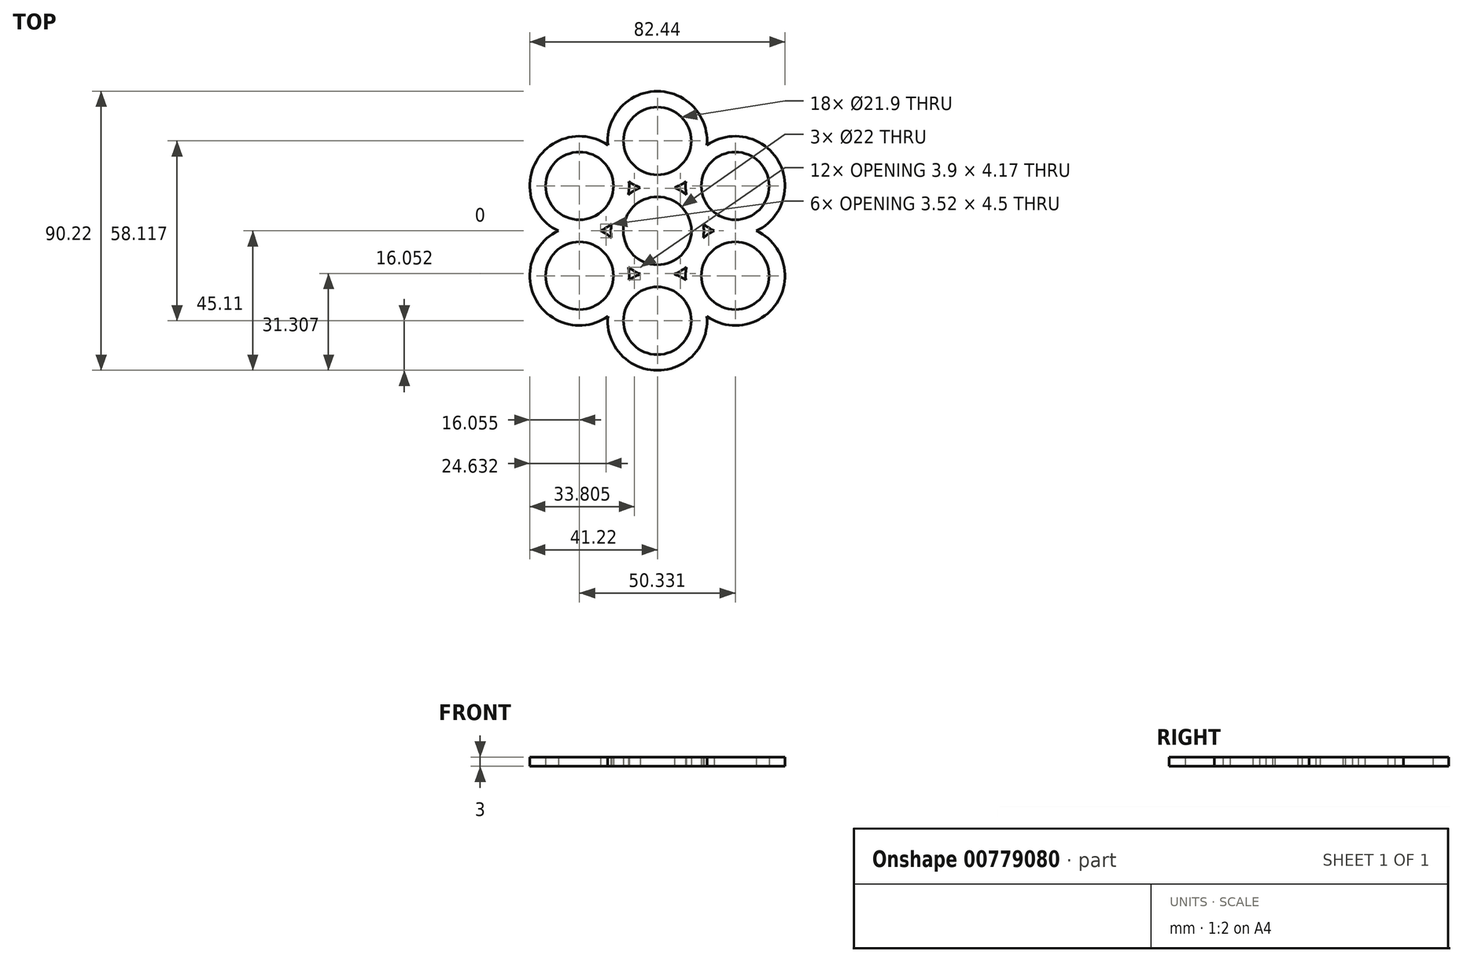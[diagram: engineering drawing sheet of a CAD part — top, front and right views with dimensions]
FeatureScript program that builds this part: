
annotation { "Feature Type Name" : "Feature", "Feature Type Description" : "" }
export const myFeature = defineFeature(function(context is Context, id is Id, definition is map)
    precondition{}
    {
        {
            var Q0;
            Q0=qCreatedBy(makeId("Top.planeOp"),FACE);
            var sketch = newSketch(context, id + "F0", { "sketchPlane" : qUnion([Q0])});
            skArc(sketch, "E0", {"start": v(5.5, 9.53) * mm, "mid": v(0, 11) * mm, "end": v(-5.5, 9.53) * mm});
            skArc(sketch, "E1", {"start": v(7.5, 13) * mm, "mid": v(6.5, 13.52) * mm, "end": v(5.47, 13.97) * mm});
            skCircle(sketch, "E2", {"center": v(0, 29.06) * mm, "radius": 10.95 * mm});
            skArc(sketch, "E3", {"start": v(16, 27.7) * mm, "mid": v(0, 45.1) * mm, "end": v(-16, 27.7) * mm});
            skArc(sketch, "E4.trimOffspring", {"start": v(-9.17, 15.89) * mm, "mid": v(-7.38, 14.8) * mm, "end": v(-5.47, 13.97) * mm});
            skArc(sketch, "E5.trimOffspring", {"start": v(5.47, 13.97) * mm, "mid": v(7.38, 14.8) * mm, "end": v(9.17, 15.89) * mm});
            skArc(sketch, "E6.trimOffspring", {"start": v(-5.47, 13.97) * mm, "mid": v(-6.5, 13.52) * mm, "end": v(-7.5, 13) * mm});
            skCircle(sketch, "E7.1.0", {"center": v(-25.17, 14.53) * mm, "radius": 10.95 * mm});
            skArc(sketch, "E7.1.1", {"start": v(-16, 27.7) * mm, "mid": v(-39.07, 22.55) * mm, "end": v(-31.98, 0) * mm});
            skArc(sketch, "E7.1.2", {"start": v(-9.36, 11.72) * mm, "mid": v(-9.13, 13.8) * mm, "end": v(-9.17, 15.89) * mm});
            skArc(sketch, "E7.1.3", {"start": v(-7.5, 13) * mm, "mid": v(-8.46, 12.39) * mm, "end": v(-9.36, 11.72) * mm});
            skArc(sketch, "E7.1.4", {"start": v(-5.5, 9.53) * mm, "mid": v(-9.53, 5.5) * mm, "end": v(-11, 0) * mm});
            skArc(sketch, "E7.1.5", {"start": v(-14.83, 2.25) * mm, "mid": v(-14.96, 1.13) * mm, "end": v(-15, 0) * mm});
            skArc(sketch, "E7.1.6", {"start": v(-18.35, 0) * mm, "mid": v(-16.51, 1) * mm, "end": v(-14.83, 2.25) * mm});
            skCircle(sketch, "E7.2.0", {"center": v(-25.17, -14.53) * mm, "radius": 10.95 * mm});
            skArc(sketch, "E7.2.1", {"start": v(-31.98, 0) * mm, "mid": v(-39.07, -22.55) * mm, "end": v(-16, -27.7) * mm});
            skArc(sketch, "E7.2.2", {"start": v(-14.83, -2.25) * mm, "mid": v(-16.51, -1) * mm, "end": v(-18.35, 0) * mm});
            skArc(sketch, "E7.2.3", {"start": v(-15, 0) * mm, "mid": v(-14.96, -1.13) * mm, "end": v(-14.83, -2.25) * mm});
            skArc(sketch, "E7.2.4", {"start": v(-11, 0) * mm, "mid": v(-9.53, -5.5) * mm, "end": v(-5.5, -9.53) * mm});
            skArc(sketch, "E7.2.5", {"start": v(-9.36, -11.72) * mm, "mid": v(-8.46, -12.39) * mm, "end": v(-7.5, -13) * mm});
            skArc(sketch, "E7.2.6", {"start": v(-9.17, -15.89) * mm, "mid": v(-9.13, -13.8) * mm, "end": v(-9.36, -11.72) * mm});
            skCircle(sketch, "E7.3.0", {"center": v(0, -29.06) * mm, "radius": 10.95 * mm});
            skArc(sketch, "E7.3.1", {"start": v(-16, -27.7) * mm, "mid": v(0, -45.1) * mm, "end": v(16, -27.7) * mm});
            skArc(sketch, "E7.3.2", {"start": v(-5.47, -13.97) * mm, "mid": v(-7.38, -14.8) * mm, "end": v(-9.17, -15.89) * mm});
            skArc(sketch, "E7.3.3", {"start": v(-7.5, -13) * mm, "mid": v(-6.5, -13.52) * mm, "end": v(-5.47, -13.97) * mm});
            skArc(sketch, "E7.3.4", {"start": v(-5.5, -9.53) * mm, "mid": v(0, -11) * mm, "end": v(5.5, -9.53) * mm});
            skArc(sketch, "E7.3.5", {"start": v(5.47, -13.97) * mm, "mid": v(6.5, -13.52) * mm, "end": v(7.5, -13) * mm});
            skArc(sketch, "E7.3.6", {"start": v(9.17, -15.89) * mm, "mid": v(7.38, -14.8) * mm, "end": v(5.47, -13.97) * mm});
            skCircle(sketch, "E7.4.0", {"center": v(25.17, -14.53) * mm, "radius": 10.95 * mm});
            skArc(sketch, "E7.4.1", {"start": v(16, -27.7) * mm, "mid": v(39.07, -22.55) * mm, "end": v(31.98, 0) * mm});
            skArc(sketch, "E7.4.2", {"start": v(9.36, -11.72) * mm, "mid": v(9.13, -13.8) * mm, "end": v(9.17, -15.89) * mm});
            skArc(sketch, "E7.4.3", {"start": v(7.5, -13) * mm, "mid": v(8.46, -12.39) * mm, "end": v(9.36, -11.72) * mm});
            skArc(sketch, "E7.4.4", {"start": v(5.5, -9.53) * mm, "mid": v(9.53, -5.5) * mm, "end": v(11, 0) * mm});
            skArc(sketch, "E7.4.5", {"start": v(14.83, -2.25) * mm, "mid": v(14.96, -1.13) * mm, "end": v(15, 0) * mm});
            skArc(sketch, "E7.4.6", {"start": v(18.35, 0) * mm, "mid": v(16.51, -1) * mm, "end": v(14.83, -2.25) * mm});
            skCircle(sketch, "E7.5.0", {"center": v(25.17, 14.53) * mm, "radius": 10.95 * mm});
            skArc(sketch, "E7.5.1", {"start": v(31.98, 0) * mm, "mid": v(39.07, 22.55) * mm, "end": v(16, 27.7) * mm});
            skArc(sketch, "E7.5.2", {"start": v(14.83, 2.25) * mm, "mid": v(16.51, 1) * mm, "end": v(18.35, 0) * mm});
            skArc(sketch, "E7.5.3", {"start": v(15, 0) * mm, "mid": v(14.96, 1.13) * mm, "end": v(14.83, 2.25) * mm});
            skArc(sketch, "E7.5.4", {"start": v(11, 0) * mm, "mid": v(9.53, 5.5) * mm, "end": v(5.5, 9.53) * mm});
            skArc(sketch, "E7.5.5", {"start": v(9.36, 11.72) * mm, "mid": v(8.46, 12.39) * mm, "end": v(7.5, 13) * mm});
            skArc(sketch, "E7.5.6", {"start": v(9.17, 15.89) * mm, "mid": v(9.13, 13.8) * mm, "end": v(9.36, 11.72) * mm});
            skSolve(sketch);
        }
        {
            var Q0;
            Q0=makeQuery(id+"F0.imprint","IMPRINT",FACE,{"disambiguationData":[TD([[makeQuery(id+"F0.imprint","IMPRINT",EDGE,{"derivedFrom":sQuery(id+"F0.wireOp",EDGE,"E0")}),-1.0]])]});
            extrude(context, id + "F1", {"entities" : qUnion([Q0]), "depth" : 3 * mm, "offsetDistance" : 25 * mm});
        }
    });
